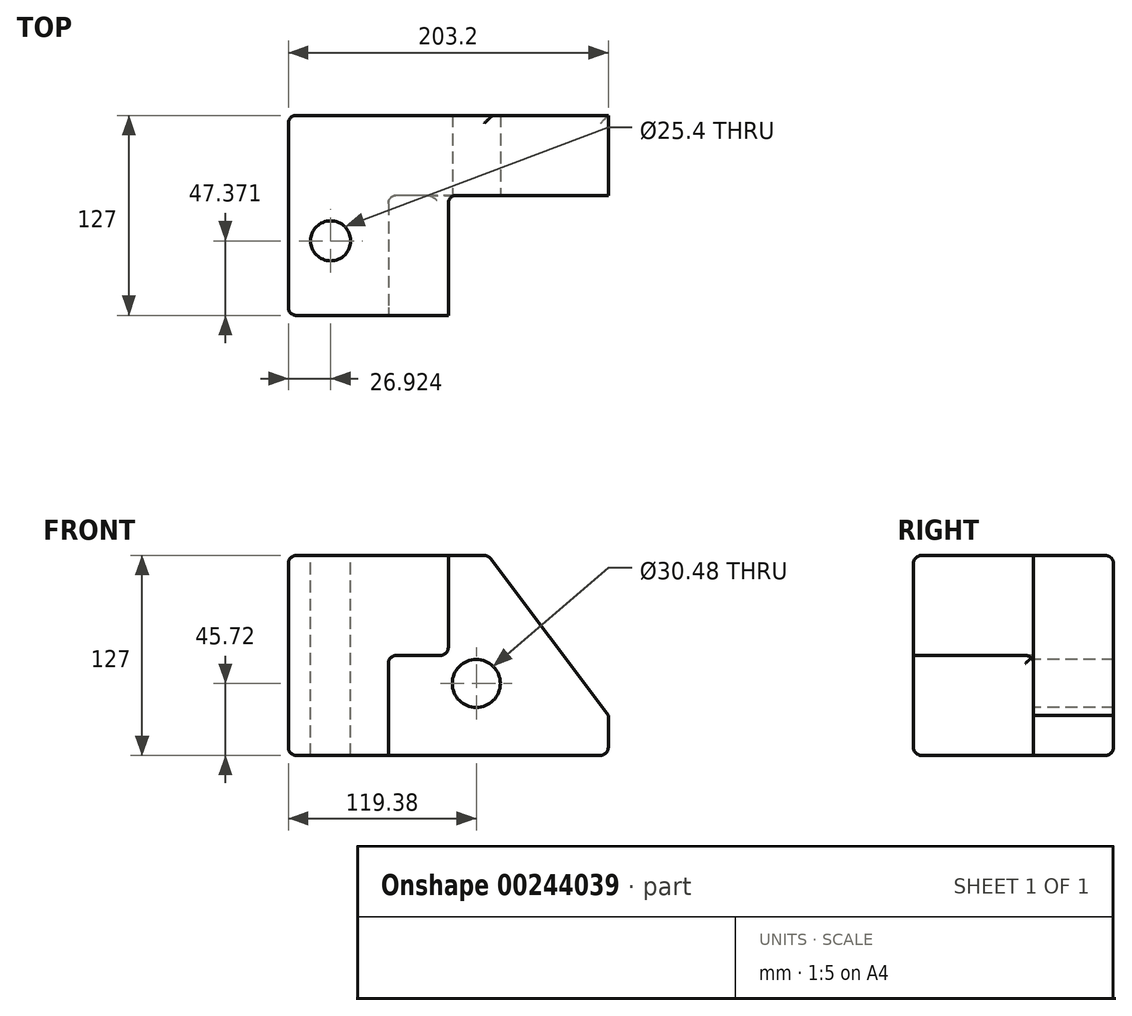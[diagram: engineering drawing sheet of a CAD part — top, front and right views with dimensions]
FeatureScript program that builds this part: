
annotation { "Feature Type Name" : "Feature", "Feature Type Description" : "" }
export const myFeature = defineFeature(function(context is Context, id is Id, definition is map)
    precondition{}
    {
        {
            var Q0;
            Q0=qCreatedBy(makeId("Front.planeOp"),FACE);
            var sketch = newSketch(context, id + "F0", { "sketchPlane" : qUnion([Q0])});
            skLineSegment(sketch, "E0.bottom", {"start": v(101.6, -63.5) * mm, "end": v(-101.6, -63.5) * mm});
            skLineSegment(sketch, "E0.top", {"start": v(101.6, 63.5) * mm, "end": v(-101.6, 63.5) * mm});
            skLineSegment(sketch, "E0.left", {"start": v(101.6, -63.5) * mm, "end": v(101.6, 63.5) * mm});
            skLineSegment(sketch, "E0.right", {"start": v(-101.6, -63.5) * mm, "end": v(-101.6, 63.5) * mm});
            skPoint(sketch, "E0.middle", {"position": v(0, 0) * mm});
            skSolve(sketch);
        }
        {
            var Q0;
            Q0=makeQuery(id+"F0.imprint","IMPRINT",FACE,{"disambiguationData":[TD([[makeQuery(id+"F0.imprint","IMPRINT",EDGE,{"derivedFrom":sQuery(id+"F0.wireOp",EDGE,"E0.bottom")}),-1.0]])]});
            extrude(context, id + "F1", {"entities" : qUnion([Q0]), "depth" : 127 * mm});
        }
        {
            var Q0;
            Q0=makeQuery(id+"F1.opExtrude","CAP_FACE",FACE,{"disambiguationData":[OSD([sQuery(id+"F0.wireOp",EDGE,"E0.bottom"),sQuery(id+"F0.wireOp",EDGE,"E0.top"),sQuery(id+"F0.wireOp",EDGE,"E0.left"),sQuery(id+"F0.wireOp",EDGE,"E0.right")])],"isStart":false});
            var sketch = newSketch(context, id + "F2", { "sketchPlane" : qUnion([Q0])});
            skLineSegment(sketch, "E1", {"start": v(-101.6, -63.5) * mm, "end": v(-38.1, -63.5) * mm});
            skLineSegment(sketch, "E2", {"start": v(0, 63.5) * mm, "end": v(0, 0) * mm});
            skLineSegment(sketch, "E3", {"start": v(0, 0) * mm, "end": v(-38.1, 0) * mm});
            skLineSegment(sketch, "E4", {"start": v(-38.1, 0) * mm, "end": v(-38.1, -63.5) * mm});
            skSolve(sketch);
        }
        {
            var Q0;
            {var subQ3=sQuery(id+"F2.wireOp",EDGE,"E2");Q0=makeQuery(id+"F2.imprint","IMPRINT",FACE,{"disambiguationData":[TD([[makeQuery(id+"F2.imprint","IMPRINT",EDGE,{"derivedFrom":subQ3}),1.0]])]});}
            extrude(context, id + "F3", {"entities" : qUnion([Q0]), "operationType" : NewBodyOperationType.REMOVE, "oppositeDirection" : true, "depth" : 76.2 * mm});
        }
        {
            var Q0;
            Q0=makeQuery(id+"F1.opExtrude","SWEPT_EDGE",EDGE,{"disambiguationData":[OSD([sQuery(id+"F0.wireOp",EDGE,"E0.top"),sQuery(id+"F0.wireOp",EDGE,"E0.left")])]});
            chamfer(context, id + "F4", {"entities" : qUnion([Q0]), "chamferType" : ChamferType.TWO_OFFSETS, "width1" : 76.2 * mm, "oppositeDirection" : false, "width2" : 101.6 * mm, "tangentPropagation" : true});
        }
        {
            var Q0;
            Q0=makeQuery(id+"F1.opExtrude","CAP_EDGE",EDGE,{"disambiguationData":[OSD([sQuery(id+"F0.wireOp",EDGE,"E0.top")])],"isStart":false});
            var Q1;
            Q1=makeQuery(id+"F3.boolean.opBoolean","COPY",EDGE,{"derivedFrom":makeQuery(id+"F3.opExtrude","SWEPT_EDGE",EDGE,{"disambiguationData":[OSD([sQuery(id+"F0.wireOp",EDGE,"E0.top"),sQuery(id+"F2.wireOp",EDGE,"E2")])]})});
            var Q2;
            Q2=makeQuery(id+"F3.boolean.opBoolean","COPY",EDGE,{"derivedFrom":makeQuery(id+"F3.opExtrude","CAP_EDGE",EDGE,{"disambiguationData":[OSD([sQuery(id+"F2.wireOp",EDGE,"E2")])],"isStart":false})});
            var Q3;
            {var subQ0=sQuery(id+"F0.wireOp",EDGE,"E0.top");Q3=makeQuery(id+"F4.opChamfer","BLEND_EDGE",EDGE,{"blendedFrom":[makeQuery(id+"F1.opExtrude","SWEPT_EDGE",EDGE,{"disambiguationData":[OSD([subQ0,sQuery(id+"F0.wireOp",EDGE,"E0.left")])]}),makeQuery(id+"F1.opExtrude","SWEPT_FACE",FACE,{"disambiguationData":[OSD([subQ0])]})],"blendedInto":[makeQuery(id+"F1.opExtrude","SWEPT_FACE",FACE,{"disambiguationData":[OSD([subQ0])]})]});}
            var Q4;
            Q4=makeQuery(id+"F1.opExtrude","CAP_EDGE",EDGE,{"disambiguationData":[OSD([sQuery(id+"F0.wireOp",EDGE,"E0.top")])],"isStart":true});
            var Q5;
            Q5=makeQuery(id+"F1.opExtrude","SWEPT_EDGE",EDGE,{"disambiguationData":[OSD([sQuery(id+"F0.wireOp",EDGE,"E0.top"),sQuery(id+"F0.wireOp",EDGE,"E0.right")])]});
            var Q6;
            Q6=makeQuery(id+"F3.boolean.opBoolean","COPY",EDGE,{"derivedFrom":makeQuery(id+"F3.opExtrude","CAP_EDGE",EDGE,{"disambiguationData":[OSD([sQuery(id+"F2.wireOp",EDGE,"E2")])],"isStart":true})});
            var Q7;
            Q7=makeQuery(id+"F3.boolean.opBoolean","COPY",EDGE,{"derivedFrom":makeQuery(id+"F3.opExtrude","CAP_EDGE",EDGE,{"disambiguationData":[OSD([sQuery(id+"F2.wireOp",EDGE,"E3")])],"isStart":true})});
            var Q8;
            Q8=makeQuery(id+"F3.boolean.opBoolean","COPY",EDGE,{"derivedFrom":makeQuery(id+"F3.opExtrude","SWEPT_EDGE",EDGE,{"disambiguationData":[OSD([sQuery(id+"F2.wireOp",EDGE,"E2"),sQuery(id+"F2.wireOp",EDGE,"E3")])]})});
            var Q9;
            Q9=makeQuery(id+"F3.boolean.opBoolean","COPY",EDGE,{"derivedFrom":makeQuery(id+"F3.opExtrude","CAP_EDGE",EDGE,{"disambiguationData":[OSD([sQuery(id+"F2.wireOp",EDGE,"E4")])],"isStart":true})});
            var Q10;
            Q10=makeQuery(id+"F3.boolean.opBoolean","COPY",EDGE,{"derivedFrom":makeQuery(id+"F3.opExtrude","CAP_EDGE",EDGE,{"disambiguationData":[OSD([sQuery(id+"F2.wireOp",EDGE,"E4")])],"isStart":false})});
            var Q11;
            Q11=makeQuery(id+"F3.boolean.opBoolean","COPY",EDGE,{"derivedFrom":makeQuery(id+"F3.opExtrude","SWEPT_EDGE",EDGE,{"disambiguationData":[OSD([sQuery(id+"F0.wireOp",EDGE,"E0.bottom"),sQuery(id+"F2.wireOp",EDGE,"E1"),sQuery(id+"F2.wireOp",EDGE,"E4")])]})});
            var Q12;
            Q12=makeQuery(id+"F1.opExtrude","CAP_EDGE",EDGE,{"disambiguationData":[OSD([sQuery(id+"F0.wireOp",EDGE,"E0.bottom")])],"isStart":false});
            var Q13;
            Q13=makeQuery(id+"F1.opExtrude","CAP_EDGE",EDGE,{"disambiguationData":[OSD([sQuery(id+"F0.wireOp",EDGE,"E0.right")])],"isStart":false});
            var Q14;
            Q14=makeQuery(id+"F3.boolean.opBoolean","COPY",EDGE,{"derivedFrom":makeQuery(id+"F3.opExtrude","SWEPT_EDGE",EDGE,{"disambiguationData":[OSD([sQuery(id+"F2.wireOp",EDGE,"E3"),sQuery(id+"F2.wireOp",EDGE,"E4")])]})});
            var Q15;
            Q15=makeQuery(id+"F1.opExtrude","SWEPT_EDGE",EDGE,{"disambiguationData":[OSD([sQuery(id+"F0.wireOp",EDGE,"E0.bottom"),sQuery(id+"F0.wireOp",EDGE,"E0.right")])]});
            var Q16;
            Q16=makeQuery(id+"F1.opExtrude","CAP_EDGE",EDGE,{"disambiguationData":[OSD([sQuery(id+"F0.wireOp",EDGE,"E0.bottom")])],"isStart":true});
            var Q17;
            Q17=makeQuery(id+"F1.opExtrude","SWEPT_EDGE",EDGE,{"disambiguationData":[OSD([sQuery(id+"F0.wireOp",EDGE,"E0.bottom"),sQuery(id+"F0.wireOp",EDGE,"E0.left")])]});
            var Q18;
            Q18=makeQuery(id+"F1.opExtrude","CAP_EDGE",EDGE,{"disambiguationData":[OSD([sQuery(id+"F0.wireOp",EDGE,"E0.right")])],"isStart":true});
            fillet(context, id + "F5", {"entities" : qUnion([Q0, Q1, Q2, Q3, Q4, Q5, Q6, Q7, Q8, Q9, Q10, Q11, Q12, Q13, Q14, Q15, Q16, Q17, Q18]), "radius" : 5.08 * mm, "tangentPropagation" : true, "allowEdgeOverflow" : false});
        }
        {
            var Q0;
            Q0=makeQuery(id+"F3.boolean.opBoolean","COPY",FACE,{"derivedFrom":makeQuery(id+"F3.opExtrude","CAP_FACE",FACE,{"disambiguationData":[OSD([sQuery(id+"F0.wireOp",EDGE,"E0.bottom"),sQuery(id+"F0.wireOp",EDGE,"E0.top"),sQuery(id+"F0.wireOp",EDGE,"E0.left"),sQuery(id+"F2.wireOp",EDGE,"E2"),sQuery(id+"F2.wireOp",EDGE,"E3"),sQuery(id+"F2.wireOp",EDGE,"E4")])],"isStart":false})});
            var sketch = newSketch(context, id + "F6", { "sketchPlane" : qUnion([Q0])});
            skCircle(sketch, "E5", {"center": v(17.78, -17.78) * mm, "radius": 15.24 * mm});
            skSolve(sketch);
        }
        {
            var Q0;
            Q0 = qSketchRegion(id + "F6", true);
            var Q1;
            Q1=makeQuery(id+"F1.opExtrude","CAP_FACE",FACE,{"disambiguationData":[OSD([sQuery(id+"F0.wireOp",EDGE,"E0.bottom"),sQuery(id+"F0.wireOp",EDGE,"E0.top"),sQuery(id+"F0.wireOp",EDGE,"E0.left"),sQuery(id+"F0.wireOp",EDGE,"E0.right")])],"isStart":true});
            extrude(context, id + "F7", {"entities" : qUnion([Q0]), "operationType" : NewBodyOperationType.REMOVE, "endBound" : BoundingType.UP_TO_SURFACE, "oppositeDirection" : true, "endBoundEntityFace" : qUnion([Q1]), "depth" : 25.4 * mm});
        }
        {
            var Q0;
            Q0=makeQuery(id+"F1.opExtrude","SWEPT_FACE",FACE,{"disambiguationData":[OSD([sQuery(id+"F0.wireOp",EDGE,"E0.top")])]});
            var sketch = newSketch(context, id + "F8", { "sketchPlane" : qUnion([Q0])});
            skCircle(sketch, "E6", {"center": v(-74.68, -79.63) * mm, "radius": 12.7 * mm});
            skSolve(sketch);
        }
        {
            var Q0;
            Q0=makeQuery(id+"F8.imprint","IMPRINT",FACE,{"disambiguationData":[TD([[makeQuery(id+"F8.imprint","IMPRINT",EDGE,{"derivedFrom":sQuery(id+"F8.wireOp",EDGE,"E6")}),1.0]])]});
            var Q1;
            Q1=makeQuery(id+"F1.opExtrude","SWEPT_FACE",FACE,{"disambiguationData":[OSD([sQuery(id+"F0.wireOp",EDGE,"E0.bottom")])]});
            extrude(context, id + "F9", {"entities" : qUnion([Q0]), "operationType" : NewBodyOperationType.REMOVE, "endBound" : BoundingType.UP_TO_SURFACE, "oppositeDirection" : true, "endBoundEntityFace" : qUnion([Q1]), "depth" : 25.4 * mm});
        }
    });
